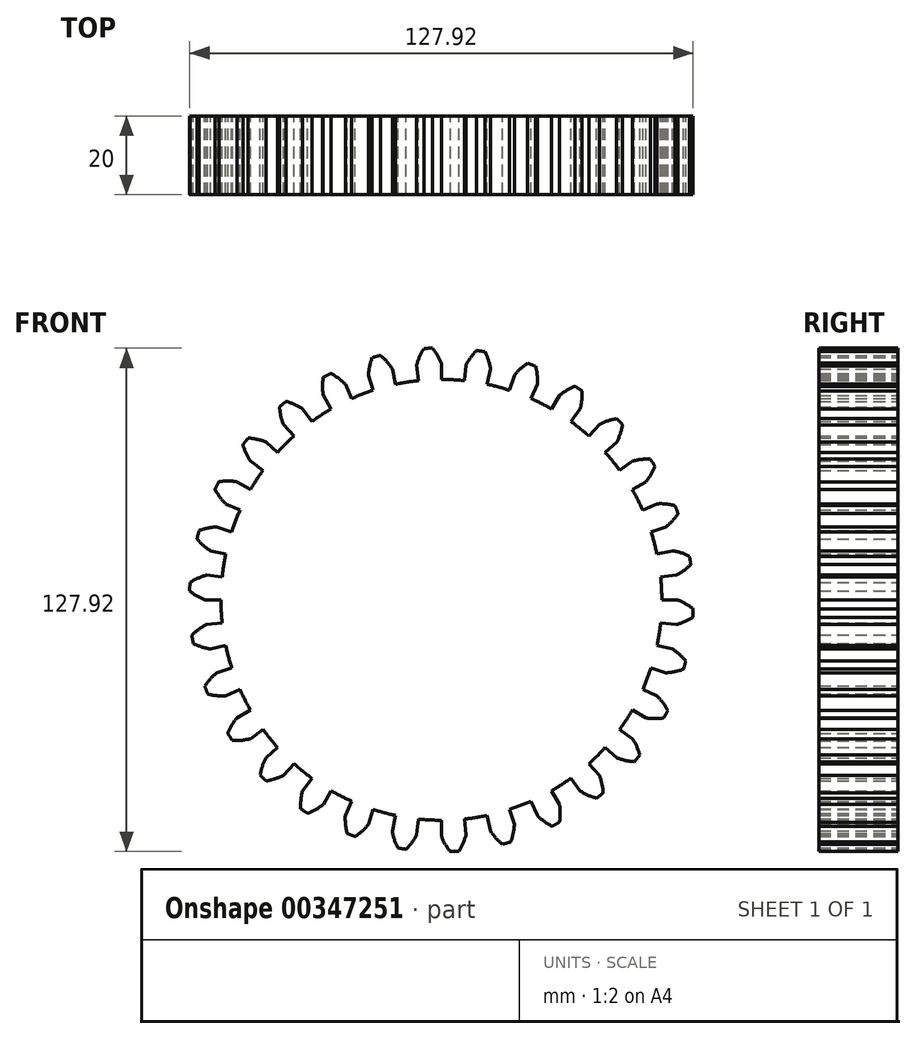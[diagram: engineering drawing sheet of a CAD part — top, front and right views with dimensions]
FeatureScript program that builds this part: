
annotation { "Feature Type Name" : "Feature", "Feature Type Description" : "" }
export const myFeature = defineFeature(function(context is Context, id is Id, definition is map)
    precondition{}
    {
        {
            assignVariable(context, id + "F0", {"name" : "N", "anyValue" : 30});
        }
        {
            var Q0;
            Q0=qCreatedBy(makeId("Front.planeOp"),FACE);
            var sketch = newSketch(context, id + "F1", { "sketchPlane" : qUnion([Q0])});
            skCircle(sketch, "E0", {"center": v(0, 0) * mm, "radius": 56 * mm});
            skCircle(sketch, "E1", {"center": v(0, 0) * mm, "radius": 60 * mm, "construction": true});
            skCircle(sketch, "E2", {"center": v(0, 0) * mm, "radius": 64 * mm, "construction": true});
            skLineSegment(sketch, "E3", {"start": v(0, 76.17) * mm, "end": v(0, 0) * mm, "construction": true});
            skLineSegment(sketch, "E4", {"start": v(-7.96, 75.75) * mm, "end": v(0, 0) * mm, "construction": true});
            skLineSegment(sketch, "E5", {"start": v(0, 60) * mm, "end": v(-23.02, 60) * mm, "construction": true});
            skLineSegment(sketch, "E6", {"start": v(-23.02, 60) * mm, "end": v(-23.02, 51.62) * mm, "construction": true});
            skLineSegment(sketch, "E7", {"start": v(-23.02, 51.62) * mm, "end": v(0, 60) * mm, "construction": true});
            skLineSegment(sketch, "E8", {"start": v(-7.96, 75.75) * mm, "end": v(0, 76.17) * mm, "construction": true});
            skLineSegment(sketch, "E9", {"start": v(0, 0) * mm, "end": v(-3.98, 75.96) * mm, "construction": true});
            skCircle(sketch, "E10", {"center": v(0, 0) * mm, "radius": 56.38 * mm, "construction": true});
            skCircle(sketch, "E11", {"center": v(0, 60) * mm, "radius": 15 * mm, "construction": true});
            skCircle(sketch, "E12", {"center": v(-14, 54.62) * mm, "radius": 15 * mm, "construction": true});
            skArc(sketch, "E13", {"start": v(-2.27, 63.96) * mm, "mid": v(-2.8, 63.94) * mm, "end": v(-3.35, 63.91) * mm});
            skArc(sketch, "E14", {"start": v(0, 60) * mm, "mid": v(-0.98, 62.07) * mm, "end": v(-2.27, 63.96) * mm});
            skLineSegment(sketch, "E15", {"start": v(0, 60) * mm, "end": v(0, 56) * mm});
            skArc(sketch, "E16.MirrorCS", {"start": v(-4.43, 63.85) * mm, "mid": v(-3.9, 63.88) * mm, "end": v(-3.35, 63.91) * mm});
            skArc(sketch, "E17.MirrorCS", {"start": v(-6.27, 59.67) * mm, "mid": v(-5.51, 61.83) * mm, "end": v(-4.43, 63.85) * mm});
            skLineSegment(sketch, "E18.MirrorCS", {"start": v(-6.27, 59.67) * mm, "end": v(-5.85, 55.7) * mm});
            skSolve(sketch);
        }
        {
            var Q0;
            {var subQ0=sQuery(id+"F1.wireOp",EDGE,"E0");var subQ1=makeQuery(id+"F1.imprint","INTERSECT",VERTEX,{"derivedFrom":[subQ0,sQuery(id+"F1.wireOp",EDGE,"E15")]});Q0=makeQuery(id+"F1.imprint","IMPRINT",FACE,{"disambiguationData":[TD([[makeQuery(id+"F1.imprint","IMPRINT",EDGE,{"disambiguationData":[TD([[subQ1,-1.0]])],"derivedFrom":subQ0}),1.0]])]});}
            var Q1;
            Q1=makeQuery(id+"F1.imprint","IMPRINT",FACE,{"disambiguationData":[TD([[makeQuery(id+"F1.imprint","IMPRINT",EDGE,{"derivedFrom":sQuery(id+"F1.wireOp",EDGE,"E13")}),1.0]])]});
            extrude(context, id + "F2", {"entities" : qUnion([Q0, Q1]), "depth" : 20 * mm, "symmetric" : true});
        }
        {
            var Q0;
            Q0=makeQuery(id+"F2.opExtrude","SWEPT_FACE",FACE,{"disambiguationData":[OSD([sQuery(id+"F1.wireOp",EDGE,"E18.MirrorCS")])]});
            var Q1;
            Q1=makeQuery(id+"F2.opExtrude","SWEPT_FACE",FACE,{"disambiguationData":[OSD([sQuery(id+"F1.wireOp",EDGE,"E17.MirrorCS")])]});
            var Q2;
            Q2=makeQuery(id+"F2.opExtrude","SWEPT_FACE",FACE,{"disambiguationData":[OSD([sQuery(id+"F1.wireOp",EDGE,"E13"),sQuery(id+"F1.wireOp",EDGE,"E16.MirrorCS")])]});
            var Q3;
            Q3=makeQuery(id+"F2.opExtrude","SWEPT_FACE",FACE,{"disambiguationData":[OSD([sQuery(id+"F1.wireOp",EDGE,"E14")])]});
            var Q4;
            Q4=makeQuery(id+"F2.opExtrude","SWEPT_FACE",FACE,{"disambiguationData":[OSD([sQuery(id+"F1.wireOp",EDGE,"E15")])]});
            var Q5;
            Q5=makeQuery(id+"F2.opExtrude","SWEPT_FACE",FACE,{"disambiguationData":[OSD([sQuery(id+"F1.wireOp",EDGE,"E0")])]});
            circularPattern(context, id + "F3", {"patternType" : PatternType.FACE, "faces" : qUnion([Q0, Q1, Q2, Q3, Q4]), "axis" : qUnion([Q5]), "angle" : 360 * degree, "instanceCount" : getVariable(context, 'N'), "equalSpace" : true});
        }
    });
